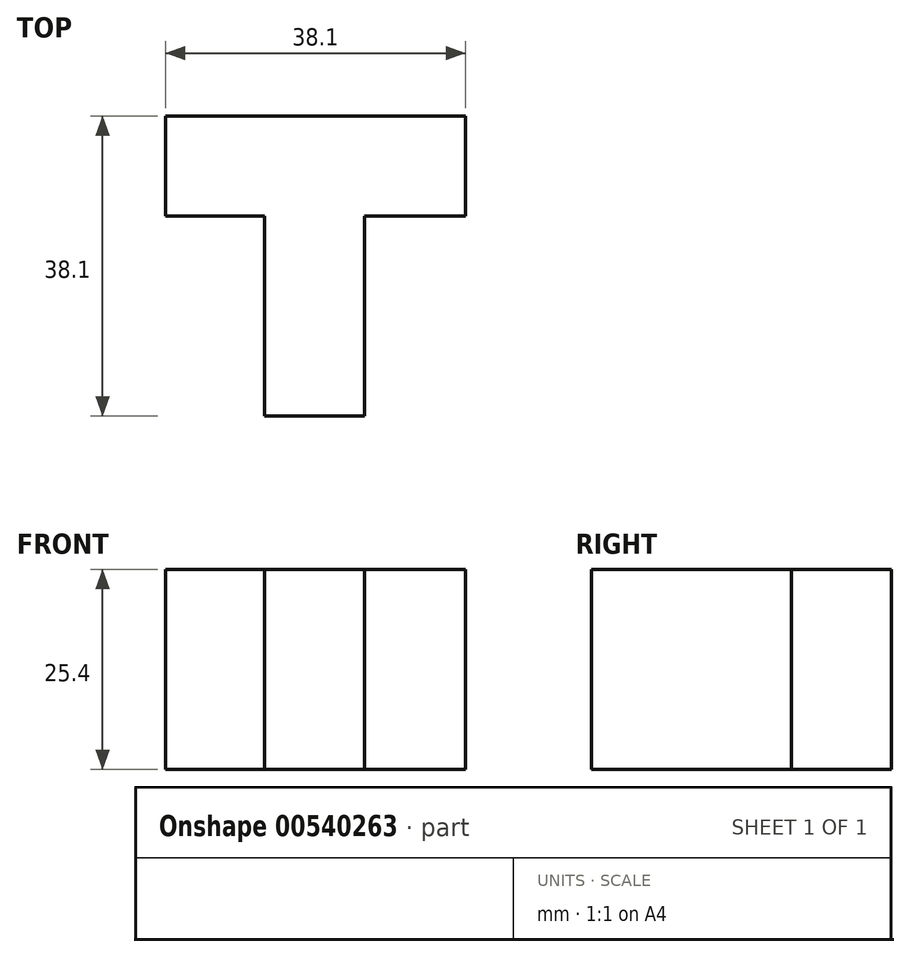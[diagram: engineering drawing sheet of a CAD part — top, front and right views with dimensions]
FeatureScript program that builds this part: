
annotation { "Feature Type Name" : "Feature", "Feature Type Description" : "" }
export const myFeature = defineFeature(function(context is Context, id is Id, definition is map)
    precondition{}
    {
        {
            var Q0;
            Q0=qCreatedBy(makeId("Top.planeOp"),FACE);
            var sketch = newSketch(context, id + "F0", { "sketchPlane" : qUnion([Q0])});
            skLineSegment(sketch, "E0", {"start": v(-65.5, 38.1) * mm, "end": v(-27.4, 38.1) * mm});
            skLineSegment(sketch, "E1", {"start": v(-27.4, 38.1) * mm, "end": v(-27.4, 25.4) * mm});
            skLineSegment(sketch, "E2", {"start": v(-27.4, 25.4) * mm, "end": v(-40.25, 25.4) * mm});
            skLineSegment(sketch, "E3", {"start": v(-40.25, 25.4) * mm, "end": v(-40.25, 0) * mm});
            skLineSegment(sketch, "E4", {"start": v(-65.5, 38.1) * mm, "end": v(-65.5, 25.4) * mm});
            skLineSegment(sketch, "E5", {"start": v(-65.5, 25.4) * mm, "end": v(-52.95, 25.4) * mm});
            skLineSegment(sketch, "E6", {"start": v(-52.95, 25.4) * mm, "end": v(-52.95, 0) * mm});
            skLineSegment(sketch, "E7", {"start": v(-52.95, 0) * mm, "end": v(-40.25, 0) * mm});
            skSolve(sketch);
        }
        {
            var Q0;
            Q0=makeQuery(id+"F0.imprint","IMPRINT",FACE,{"disambiguationData":[TD([[makeQuery(id+"F0.imprint","IMPRINT",EDGE,{"derivedFrom":sQuery(id+"F0.wireOp",EDGE,"E0")}),-1.0]])]});
            extrude(context, id + "F1", {"entities" : qUnion([Q0]), "depth" : 25.4 * mm, "offsetDistance" : 25.4 * mm});
        }
    });
